# Revit family: JOMA_Balksko kombi_Grundform 440
name_source: partatom
category: Structural Connections
revit_build: Autodesk Revit Structure 2012 (Build: 20110309_2315(x64)
units: mm (PartAtom-declared; Revit-internal decimal feet)

## types (8) — shared parameters
D = 42 mm  [stored 0.137795 ft]
Default Elevation = 1219 mm
E = 47 mm  [stored 0.154199 ft]
F = 85 mm  [stored 0.278871 ft]
Grundform 440 = Yes
Länk Joma Dimensioneringsverktyg = http://www.joma.se
Material = Varmförzinkad stålplåt
Typ = GRUNDFORM 440
X = 35 mm  [stored 0.114829 ft]
Y = 110 mm  [stored 0.360892 ft]

## per-type parameters (varying)
| type | A | B | Vikt |
| 5245197  45x197 | 45 mm  [stored 0.147638 ft] | 197 mm | 0,54 |
| 5251195  51x195 | 51 mm | 195 mm  [stored 0.639764 ft] | 0,54 |
| 5276182  76x182 | 76 mm  [stored 0.249344 ft] | 182 mm  [stored 0.597113 ft] | 0,43 |
| 5280180  80x180 | 80 mm  [stored 0.262467 ft] | 180 mm  [stored 0.590551 ft] | 0,54 |
| 5210170  100x170 | 100 mm  [stored 0.328084 ft] | 170 mm  [stored 0.557743 ft] | 0,54 |
| 5215162  115x162 | 115 mm  [stored 0.377297 ft] | 162 mm  [stored 0.531496 ft] | 0,54 |
| 5212160  120x160 | 120 mm  [stored 0.393701 ft] | 160 mm  [stored 0.524934 ft] | 0,54 |
| 5260190  60x190 | 60 mm  [stored 0.19685 ft] | 190 mm | 0,54 |

note: [stored X ft] marks values corroborated as IEEE doubles in the binary element streams (Revit-internal decimal feet)

## geometry (parser evidence)
native form markers: Sweep x1
no freeform markers — native parametric forms only
